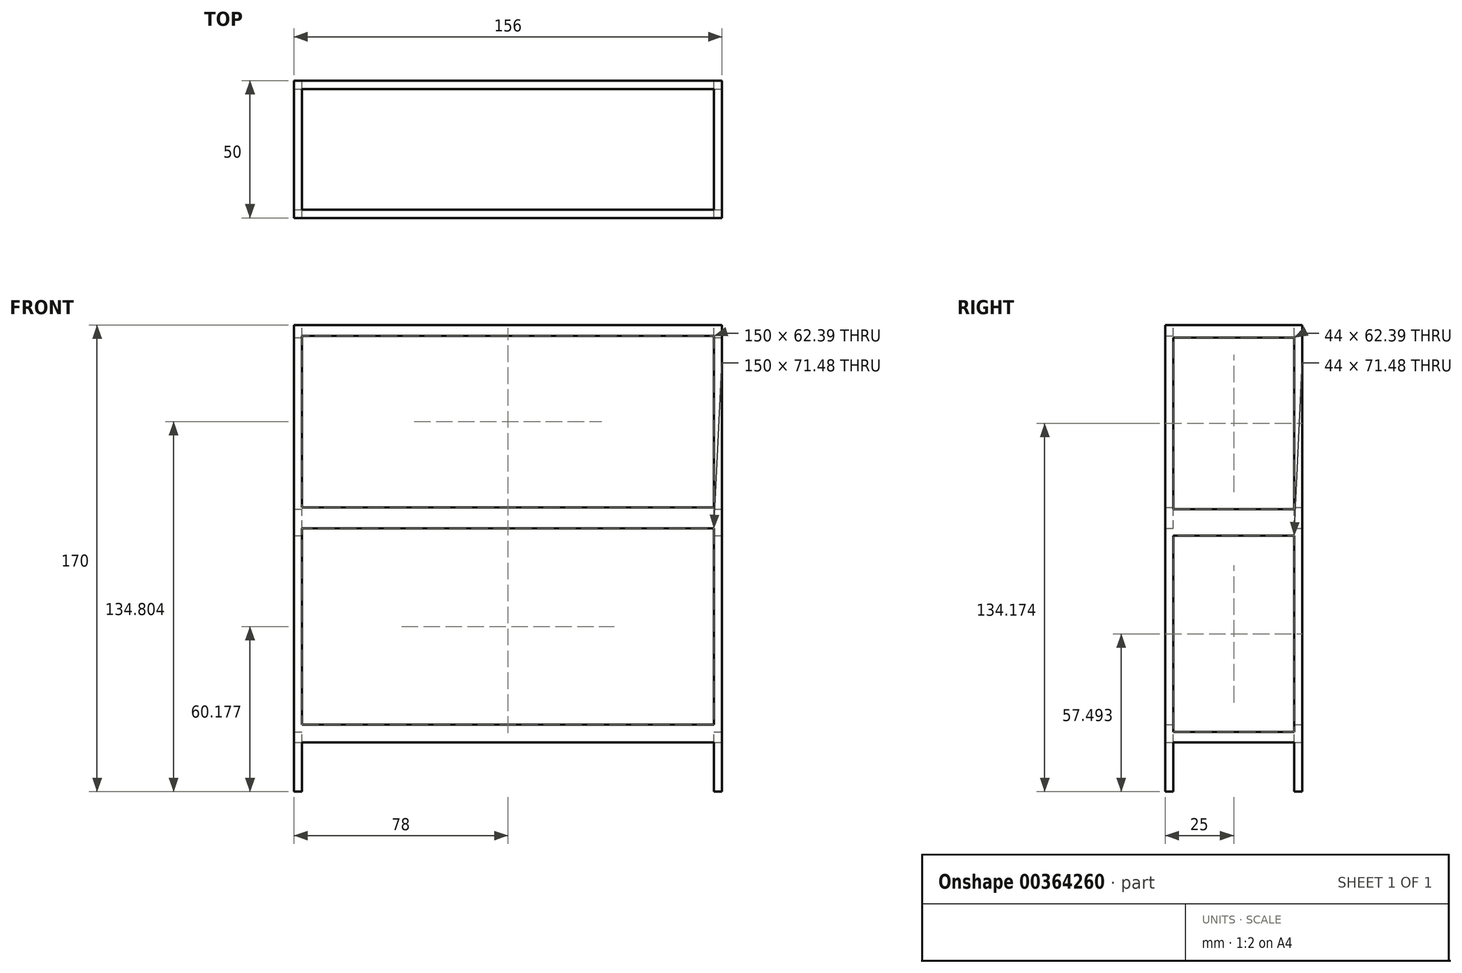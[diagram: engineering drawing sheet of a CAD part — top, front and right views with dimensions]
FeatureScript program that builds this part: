
annotation { "Feature Type Name" : "Feature", "Feature Type Description" : "" }
export const myFeature = defineFeature(function(context is Context, id is Id, definition is map)
    precondition{}
    {
        {
            var Q0;
            Q0=qCreatedBy(makeId("Front.planeOp"),FACE);
            var sketch = newSketch(context, id + "F0", { "sketchPlane" : qUnion([Q0])});
            skPoint(sketch, "E0", {"position": v(-74.5, -100) * mm});
            skPoint(sketch, "E1", {"position": v(-74.5, -80) * mm});
            skPoint(sketch, "E2", {"position": v(-74.5, 0) * mm});
            skPoint(sketch, "E3", {"position": v(-74.5, 70) * mm});
            skLineSegment(sketch, "E4", {"start": v(-74.5, 70) * mm, "end": v(-74.5, -100) * mm});
            skLineSegment(sketch, "E5.MirrorCS", {"start": v(81.5, 70) * mm, "end": v(81.5, -100) * mm});
            skLineSegment(sketch, "E6", {"start": v(-74.5, -100) * mm, "end": v(81.5, -100) * mm});
            skLineSegment(sketch, "E7", {"start": v(-74.5, -80) * mm, "end": v(81.5, -80) * mm});
            skLineSegment(sketch, "E8", {"start": v(-74.5, 0) * mm, "end": v(81.5, 0) * mm});
            skLineSegment(sketch, "E9", {"start": v(-74.5, 70) * mm, "end": v(81.5, 70) * mm});
            skSolve(sketch);
        }
        {
            var Q0;
            Q0 = qSketchRegion(id + "F0", true);
            extrude(context, id + "F1", {"entities" : qUnion([Q0]), "oppositeDirection" : true, "depth" : 50 * mm});
        }
        {
            var Q0;
            Q0=makeQuery(id+"F1.opExtrude","CAP_FACE",FACE,{"disambiguationData":[OSD([sQuery(id+"F0.wireOp",EDGE,"E4"),sQuery(id+"F0.wireOp",EDGE,"E5.MirrorCS"),sQuery(id+"F0.wireOp",EDGE,"ZChAxPbI-4E8A-uPK1-GYCJ-lD4HdbXtsLgx"),sQuery(id+"F0.wireOp",EDGE,"RT3eMIAg-hPzZ-fsc6-fuXe-IxCWJ52PeQDx")])],"isStart":false});
            var sketch = newSketch(context, id + "F2", { "sketchPlane" : qUnion([Q0])});
            skLineSegment(sketch, "E10.bottom", {"start": v(-78.5, -100) * mm, "end": v(71.5, -100) * mm});
            skLineSegment(sketch, "E10.top", {"start": v(-78.5, -82.1) * mm, "end": v(71.5, -82.1) * mm});
            skLineSegment(sketch, "E10.left", {"start": v(-78.5, -100) * mm, "end": v(-78.5, -82.1) * mm});
            skLineSegment(sketch, "E10.right", {"start": v(71.5, -100) * mm, "end": v(71.5, -82.1) * mm});
            skLineSegment(sketch, "E11.bottom", {"start": v(-78.5, -75.56) * mm, "end": v(71.5, -75.56) * mm});
            skLineSegment(sketch, "E11.top", {"start": v(-78.5, -4.08) * mm, "end": v(71.5, -4.08) * mm});
            skLineSegment(sketch, "E11.left", {"start": v(-78.5, -75.56) * mm, "end": v(-78.5, -4.08) * mm});
            skLineSegment(sketch, "E11.right", {"start": v(71.5, -75.56) * mm, "end": v(71.5, -4.08) * mm});
            skLineSegment(sketch, "E12.bottom", {"start": v(71.5, 3.6) * mm, "end": v(-78.5, 3.6) * mm});
            skLineSegment(sketch, "E12.top", {"start": v(71.5, 66) * mm, "end": v(-78.5, 66) * mm});
            skLineSegment(sketch, "E12.left", {"start": v(71.5, 3.6) * mm, "end": v(71.5, 66) * mm});
            skLineSegment(sketch, "E12.right", {"start": v(-78.5, 3.6) * mm, "end": v(-78.5, 66) * mm});
            skSolve(sketch);
        }
        {
            var Q0;
            Q0 = qSketchRegion(id + "F2", true);
            extrude(context, id + "F3", {"entities" : qUnion([Q0]), "operationType" : NewBodyOperationType.REMOVE, "oppositeDirection" : true, "depth" : 70 * mm});
        }
        {
            var Q0;
            Q0=makeQuery(id+"F1.opExtrude","SWEPT_FACE",FACE,{"disambiguationData":[OSD([sQuery(id+"F0.wireOp",EDGE,"E9")])]});
            var sketch = newSketch(context, id + "F4", { "sketchPlane" : qUnion([Q0])});
            skLineSegment(sketch, "E13.bottom", {"start": v(-71.5, 47) * mm, "end": v(78.5, 47) * mm});
            skLineSegment(sketch, "E13.top", {"start": v(-71.5, 3) * mm, "end": v(78.5, 3) * mm});
            skLineSegment(sketch, "E13.left", {"start": v(-71.5, 47) * mm, "end": v(-71.5, 3) * mm});
            skLineSegment(sketch, "E13.right", {"start": v(78.5, 47) * mm, "end": v(78.5, 3) * mm});
            skSolve(sketch);
        }
        {
            var Q0;
            Q0 = qSketchRegion(id + "F4", true);
            extrude(context, id + "F5", {"entities" : qUnion([Q0]), "operationType" : NewBodyOperationType.REMOVE, "oppositeDirection" : true, "depth" : 200 * mm});
        }
        {
            var Q0;
            Q0=makeQuery(id+"F1.opExtrude","SWEPT_FACE",FACE,{"disambiguationData":[OSD([sQuery(id+"F0.wireOp",EDGE,"E5.MirrorCS")])]});
            var sketch = newSketch(context, id + "F6", { "sketchPlane" : qUnion([Q0])});
            skLineSegment(sketch, "E14.bottom", {"start": v(3, -100) * mm, "end": v(47, -100) * mm});
            skLineSegment(sketch, "E14.top", {"start": v(3, -82.1) * mm, "end": v(47, -82.1) * mm});
            skLineSegment(sketch, "E14.left", {"start": v(3, -100) * mm, "end": v(3, -82.1) * mm});
            skLineSegment(sketch, "E14.right", {"start": v(47, -100) * mm, "end": v(47, -82.1) * mm});
            skLineSegment(sketch, "E15.bottom", {"start": v(3, -78.25) * mm, "end": v(47, -78.25) * mm});
            skLineSegment(sketch, "E15.top", {"start": v(3, -6.77) * mm, "end": v(47, -6.77) * mm});
            skLineSegment(sketch, "E15.left", {"start": v(3, -78.25) * mm, "end": v(3, -6.77) * mm});
            skLineSegment(sketch, "E15.right", {"start": v(47, -78.25) * mm, "end": v(47, -6.77) * mm});
            skLineSegment(sketch, "E16.bottom", {"start": v(3, 2.98) * mm, "end": v(47, 2.98) * mm});
            skLineSegment(sketch, "E16.top", {"start": v(3, 65.37) * mm, "end": v(47, 65.37) * mm});
            skLineSegment(sketch, "E16.left", {"start": v(3, 2.98) * mm, "end": v(3, 65.37) * mm});
            skLineSegment(sketch, "E16.right", {"start": v(47, 2.98) * mm, "end": v(47, 65.37) * mm});
            skSolve(sketch);
        }
        {
            var Q0;
            Q0 = qSketchRegion(id + "F6", true);
            extrude(context, id + "F7", {"entities" : qUnion([Q0]), "operationType" : NewBodyOperationType.REMOVE, "oppositeDirection" : true, "depth" : 200 * mm});
        }
    });
